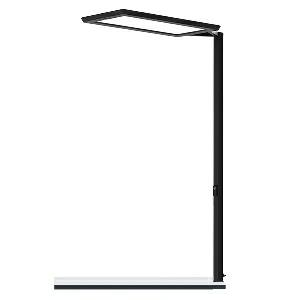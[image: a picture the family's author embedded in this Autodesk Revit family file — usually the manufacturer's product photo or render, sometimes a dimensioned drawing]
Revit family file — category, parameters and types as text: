
# Revit family: yara_single_-_yat_6000_840_r_sw_cee_00_00810200_dc29
name_source: partatom
category: Lighting Fixtures
units: mm (PartAtom-declared; Revit-internal decimal feet)

## family parameters
Cut with Voids When Loaded = No
Host = Face
Light Source = No
Part Type = Normal
Room Calculation Point = No
Round Connector Dimension = Use Diameter
Shared = No

## types (1)
- YARA.single - YAT 6000/840/R/SW/CEE/00 (1 x LED, 6000 lm, 4000K)
    Apparent Load = 42 VA
    Approval mark = CE
    CIE Flux Codes = 58 87 97 13 100
    Color Rendering = 80-89
    Color Temperature = 4000K
    Control Gear = Electronic ballast
    Default Elevation = 1800 mm
    Description = YAT 6000/840/R/SW/CEE/00/|Desk-mounted luminaire|light source: LED|work equipment: Electronic ballast DALI|connected load: 220-240 V, 50/60 Hz|Power consumption: approx. 42 W|standby: approx. 0,50|power factor: approx. 0,966|luminous flux: 6000 lm|luminous efficacy: 142 lm/W|light distribution: Direct/indirect|direct ratio: approx. 13 %|colour temperature: Cold white, ca. 4000 K|color rendering index (CRI): >= 80|chromaticity tolerance:  3 SDCM|technology: Presence and daylight sensor control (PIR)|operation: Wireless switch|luminaire body|material: Aluminium/plastic|surface: Powder coatet|colour: Black|lamp cover: Acrylic (PMMA), Satine, Structured|tubular section|material: Steel tube|surface: Powder-coated|Form: Tubular section upright|colour of tubular section: Black|weight (net): approx. 7.7 kg|mains lead: 3.00 m Mains plug CEE 7/VII|Fastening: Socket, Table adaptor|glare control: Prism aperture|luminance(L65): <= 1100 cd/m|unified glare rating(4H 8H): <=  16|special features: App control, Asymmetric radiation, Direct and indirect lighting component with edge light and light guidetechnology for a homogeneous light exit, Flicker-free, Magnetic control panel, freely positionable, PIR movement and daylight sensor|Approval mark: VDE - ENEC|
    Frequency = 50 Hz, 60 Hz
    Height = 24 mm  [stored 0.0787402 ft]
    Lamp = 1 x LED
    Lamp Light Flux = 6000 lm
    Lamp count = 1
    Length = 690 mm
    Luminous efficacy = 143 lm/W
    Manufacturer = Waldmann
    ModVariant = No
    Model = 00810200
    Mounting Place = Table
    Mounting Type = Surface mounted
    Number of Poles = 1
    OnlyDefault = Yes
    Power Factor = 1
    Product Name = YARA.single - YAT 6000/840/R/SW/CEE/00
    Product group = Desk mounted luminaire
    ProductGroupID = 22
    Protection Class = Protection class I
    Protection Degree = IP 20
    RLX_Detail_Level = 1
    RLX_Emergency_Light_Flux = 0 lm
    RLX_Emergency_Type = 0
    RLX_Emergency_Type_DB = No
    RlxData = <blob elided: 61789 chars, md5=67eae1cd>
    Socket = socket
    Standby Power = 0 W
    System Light Flux = 6000 lm
    System Power = 42 W
    Type Comments = Product without accessories
    Type Image = yat-r-sw.jpg
    URL = http://relux.com
    VarID = ---
    Voltage = 230 V
    Voltage Range = 220-240 V
    Weight = 0.00 kg
    Width = 358 mm

note: [stored X ft] marks values corroborated as IEEE doubles in the binary element streams (Revit-internal decimal feet)

## geometry (parser evidence)
native form markers: Blend x4, Sweep x14
no freeform markers — native parametric forms only
